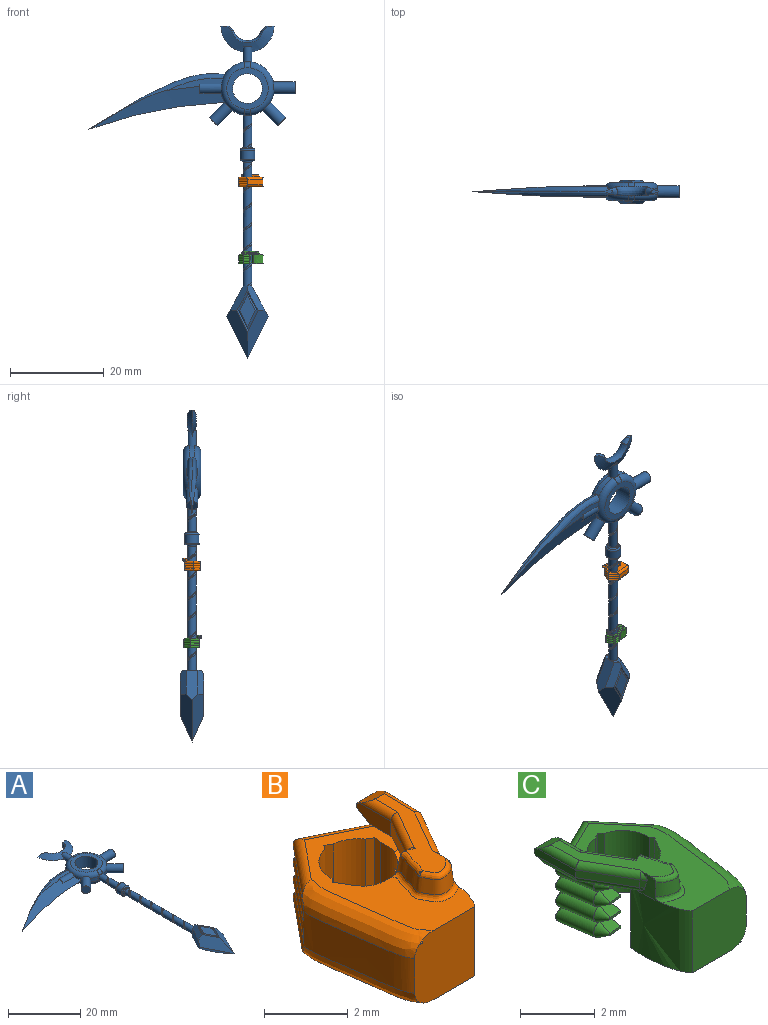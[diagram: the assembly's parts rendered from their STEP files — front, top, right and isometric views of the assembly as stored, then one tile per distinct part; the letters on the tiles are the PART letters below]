
ASSEMBLY  parts=3 mates=2
PART A: 95 faces, bbox 47.1x71.3x5.4 mm
  f0: cylinder r=0.95mm len=6.92mm, axis (0,1,0), area 36.3mm2, adj f1,f2,f3,f6,f20,f23,f67,f69
  f1: bspline ~8.16x2.41mm, area 3.9mm2, adj f0,f2,f3,f37,f38,f67,f68,f69
  f2: bspline ~8.15x2.45mm, area 3.9mm2, adj f0,f1,f20,f37,f38,f67
  f3: cylinder r=5.71mm len=2.59mm, axis (0,0,-1), area 3.2mm2, adj f0,f1,f12,f13,f35,f37
  f4: cylinder r=5.71mm len=2.11mm, axis (0,0,-1), area 0.8mm2, adj f13,f35,f40,f44
  f5: cylinder r=3.17mm len=6.35mm, axis (0,0,-1), area 76mm2, adj f16,f17
  f6: cylinder r=5.71mm len=2.59mm, axis (0,0,-1), area 3.2mm2, adj f0,f8,f9,f33
  f7: cylinder r=5.71mm len=2.11mm, axis (0,0,-1), area 2.6mm2, adj f8,f9,f25,f33
  f8: torus R=4.45mm, axis (0,0,1), area 28.3mm2, adj f6,f7,f15,f17,f20,f21,f25,f33
  f9: torus R=4.45mm, axis (0,0,1), area 28.3mm2, adj f6,f7,f15,f16,f22,f23,f25,f33
  f10: cylinder r=5.71mm len=4.27mm, axis (0,0,-1), area 6.4mm2, adj f12,f13,f19,f41,f42
  f11: cylinder r=5.71mm len=2.11mm, axis (0,0,-1), area 0.8mm2, adj f12,f35,f39,f45
  f12: torus R=4.45mm, axis (0,0,1), area 27.6mm2, adj f3,f10,f11,f17,f20,f21,f32,f35
  f13: torus R=4.45mm, axis (0,0,1), area 27.7mm2, adj f3,f4,f10,f16,f22,f23,f31,f35
  f14: plane 1.74x0.58mm, normal (0,1,0), area 0.4mm2, adj f19,f26
  f15: cylinder r=5.71mm len=4.87mm, axis (0,0,-1), area 8.6mm2, adj f8,f9,f19,f25
  f16: plane 8.97x8.89mm, normal (0,0,1), area 30.4mm2, adj f5,f9,f13,f22,f23
  f17: plane 8.97x8.89mm, normal (0,0,-1), area 30.4mm2, adj f5,f8,f12,f20,f21
  f18: plane 1.66x0.52mm, normal (0,1,0), area 0.4mm2, adj f19,f27
  f19: cylinder r=0.95mm len=3.3mm, axis (0,1,0), area 18.3mm2, adj f10,f14,f15,f18,f21,f22,f26,f27
  f20: bspline ~1.53x1.35mm, area 2.3mm2, adj f0,f2,f8,f12,f17,f37
  f21: bspline ~1.42x1.3mm, area 2.3mm2, adj f8,f12,f17,f19
  f22: bspline ~1.42x1.3mm, area 2.3mm2, adj f9,f13,f16,f19
  f23: bspline ~1.42x1.3mm, area 2.3mm2, adj f0,f9,f13,f16
  f24: plane 2.54x2.54mm, normal (1,0,0), area 5.1mm2, adj f25
  f25: cylinder r=1.27mm len=4.58mm, axis (-1,0,0), area 36.3mm2, adj f7,f8,f9,f15,f24
  f26: bspline ~11.33x5.46mm, area 29.7mm2, adj f14,f19,f27,f28,f29,f30,f93,f94
  f27: bspline ~11.33x5.46mm, area 30.2mm2, adj f18,f19,f26,f28,f29,f30,f93,f94
  f28: plane 1.88x1.27mm, normal (0.01,1,0), area 0.8mm2, adj f26,f27,f94
  f29: plane 1.84x1.25mm, normal (0.01,1,0), area 0.7mm2, adj f26,f27,f93
  f30: bspline ~7.14x7.14mm, area 18.5mm2, adj f26,f27,f93,f94
  f31: plane 12.18x2.8mm, normal (0,0,1), area 11.7mm2, adj f13,f40,f41,f43,f44
  f32: plane 12.19x2.81mm, normal (0,0,-1), area 11.7mm2, adj f12,f39,f42,f45,f46
  f33: cylinder r=1.27mm len=5.04mm, axis (-0.71,0.71,0), area 36.3mm2, adj f6,f7,f8,f9,f34
  f34: plane 2.54x1.8mm, normal (0.71,-0.71,0), area 5.1mm2, adj f33
  f35: cylinder r=1.27mm len=5.06mm, axis (0.71,0.71,0), area 36.2mm2, adj f3,f4,f11,f12,f13,f36
  f36: plane 2.54x1.8mm, normal (-0.71,-0.71,0), area 5.1mm2, adj f35
  f37: bspline ~2.13x1.59mm, area 0.5mm2, adj f1,f2,f3,f12,f20,f38
  f38: plane 0.71x0.37mm, normal (0,0,-1), area 0.1mm2, adj f1,f2,f37
  f39: bspline ~33.29x10.15mm, area 73.1mm2, adj f11,f32,f40,f42,f45,f46
  f40: bspline ~33.29x10.15mm, area 73mm2, adj f4,f31,f39,f41,f43,f44
  f41: bspline ~30.28x13.43mm, area 35.4mm2, adj f10,f13,f31,f40,f42
  f42: bspline ~30.28x13.43mm, area 35.4mm2, adj f10,f12,f32,f39,f41
  f43: plane 1.87x0.64mm, normal (-1,0,0), area 0.5mm2, adj f31,f40,f44
  f44: cylinder r=1.27mm len=4.58mm, axis (1,0,0), area 10.1mm2, adj f4,f13,f31,f40,f43
  f45: cylinder r=1.27mm len=4.58mm, axis (1,0,0), area 10.1mm2, adj f11,f12,f32,f39,f46
  f46: plane 1.87x0.64mm, normal (-1,0,0), area 0.5mm2, adj f32,f39,f45
  f47: plane 2.57x2.57mm, normal (0,1,0), area 0.2mm2, adj f67,f68,f69,f74
  f48: plane 2.57x2.57mm, normal (0,-1,0), area 0.2mm2, adj f70,f71,f72,f73
  f49: cylinder r=1.59mm len=3.18mm, axis (0,-1,0), area 19.3mm2, adj f73,f74
  f50: plane 10.2x4.46mm, normal (-0.63,-0.32,0.71), area 28.3mm2, adj f51,f53,f57,f58,f78
  f51: plane 10.2x4.46mm, normal (-0.63,-0.32,-0.71), area 28.3mm2, adj f50,f52,f55,f58,f84
  f52: plane 5.16x3.72mm, normal (-0.62,0.34,-0.71), area 10.1mm2, adj f51,f54,f58,f59,f85
  f53: plane 10.2x4.46mm, normal (0.63,-0.32,0.71), area 28.3mm2, adj f50,f55,f56,f61,f79
  f54: plane 5.16x3.72mm, normal (0.62,0.34,-0.71), area 10.1mm2, adj f52,f55,f60,f61,f86
  f55: plane 10.2x4.46mm, normal (0.63,-0.32,-0.71), area 28.3mm2, adj f51,f53,f54,f61,f91
  f56: plane 5.16x3.72mm, normal (0.62,0.34,0.71), area 10.1mm2, adj f53,f57,f61,f62,f80
  f57: plane 5.16x3.72mm, normal (-0.62,0.34,0.71), area 10.1mm2, adj f50,f56,f58,f63,f81
  f58: plane 6.48x3.56mm, normal (-0.88,0.48,0), area 16.7mm2, adj f50,f51,f52,f57,f59,f63,f66
  f59: plane 1.93x0.96mm, normal (-0.06,1,0), area 0.9mm2, adj f52,f58,f60,f66
  f60: plane 1.93x0.96mm, normal (0.06,1,0), area 0.9mm2, adj f54,f59,f61,f66
  f61: plane 6.48x3.56mm, normal (0.88,0.48,0), area 16.7mm2, adj f53,f54,f55,f56,f60,f62,f66
  f62: plane 1.94x0.96mm, normal (0.06,1,0), area 0.9mm2, adj f56,f61,f63,f64,f65,f66
  f63: plane 1.93x0.95mm, normal (-0.06,1,0), area 0.9mm2, adj f57,f58,f62,f64,f66
  f64: bspline ~28x2.45mm, area 13.4mm2, adj f62,f63,f65,f66,f70,f71,f72
  f65: bspline ~28.02x2.41mm, area 13.8mm2, adj f62,f64,f66,f71
  f66: cylinder r=0.95mm len=26.59mm, axis (0,1,0), area 134.4mm2, adj f58,f59,f60,f61,f62,f63,f64,f65
  f67: bspline ~0.85x0.81mm, area 0.2mm2, adj f0,f1,f2,f47,f68,f69
  f68: bspline ~0.61x0.46mm, area 0.1mm2, adj f1,f47,f67,f69
  f69: torus R=1.26mm, axis (0,-1,0), area 3mm2, adj f0,f1,f47,f67,f68
  f70: bspline ~0.57x0.49mm, area 0.1mm2, adj f48,f64,f71,f72
  f71: bspline ~0.85x0.75mm, area 0.2mm2, adj f48,f64,f65,f66,f70,f72
  f72: torus R=1.26mm, axis (0,-1,0), area 3mm2, adj f48,f64,f66,f70,f71
  f73: torus R=1.28mm, axis (0,-1,0), area 4.4mm2, adj f48,f49
  f74: torus R=1.28mm, axis (0,-1,0), area 4.4mm2, adj f47,f49
  f75: plane 3.66x2mm, normal (-0.62,0.34,0.71), area 1.4mm2, adj f76,f81,f82,f83
  f76: plane 3.66x2mm, normal (0.62,0.34,0.71), area 1.4mm2, adj f75,f77,f80,f83
  f77: plane 3.96x2mm, normal (0.63,-0.32,0.71), area 1.5mm2, adj f76,f79,f82,f83
  f78: plane 4.53x2.28mm, normal (0.63,0.32,0.71), area 1.7mm2, adj f50,f79,f81,f82
  f79: plane 4.53x2.28mm, normal (-0.63,0.32,0.71), area 1.7mm2, adj f53,f77,f78,f80
  f80: plane 4.18x2.28mm, normal (-0.62,-0.34,0.71), area 1.6mm2, adj f56,f76,f79,f81
  f81: plane 4.18x2.28mm, normal (0.62,-0.34,0.71), area 1.6mm2, adj f57,f75,f78,f80
  f82: plane 3.96x2mm, normal (-0.63,-0.32,0.71), area 1.5mm2, adj f75,f77,f78,f83
  f83: plane 6.52x3.42mm, normal (0,0,1), area 11.1mm2, adj f75,f76,f77,f82
  f84: plane 4.53x2.28mm, normal (0.63,0.32,-0.71), area 1.7mm2, adj f51,f85,f90,f91
  f85: plane 4.18x2.28mm, normal (0.62,-0.34,-0.71), area 1.6mm2, adj f52,f84,f86,f89
  f86: plane 4.18x2.28mm, normal (-0.62,-0.34,-0.71), area 1.6mm2, adj f54,f85,f88,f91
  f87: plane 3.96x2mm, normal (0.63,-0.32,-0.71), area 1.5mm2, adj f88,f90,f91,f92
  f88: plane 3.66x2mm, normal (0.62,0.34,-0.71), area 1.4mm2, adj f86,f87,f89,f92
  f89: plane 3.66x2mm, normal (-0.62,0.34,-0.71), area 1.4mm2, adj f85,f88,f90,f92
  f90: plane 3.96x2mm, normal (-0.63,-0.32,-0.71), area 1.5mm2, adj f84,f87,f89,f92
  f91: plane 4.53x2.28mm, normal (-0.63,0.32,-0.71), area 1.7mm2, adj f55,f84,f86,f87
  f92: plane 6.52x3.42mm, normal (0,0,-1), area 11.1mm2, adj f87,f88,f89,f90
  f93: bspline ~2.68x1.63mm, area 2.6mm2, adj f26,f27,f29,f30
  f94: bspline ~2.79x1.69mm, area 2.8mm2, adj f26,f27,f28,f30
PART B: 79 faces, bbox 4.3x5.7x2.9 mm
  f0: plane 4.84x2.76mm, normal (0,0,-1), area 6.7mm2, adj f5,f6,f7,f8,f9,f10,f12,f16
  f1: plane 0.22x0.13mm, normal (-0.98,0.2,0), area 0mm2, adj f10,f19,f23,f76
  f2: plane 0.22x0.13mm, normal (-0.98,0.2,0), area 0mm2, adj f25,f29,f30,f76
  f3: plane 0.22x0.13mm, normal (-0.98,0.2,0), area 0mm2, adj f32,f36,f37,f76
  f4: plane 0.22x0.13mm, normal (-0.98,0.2,0), area 0mm2, adj f39,f43,f44,f76
  f5: plane 2.03x0.23mm, normal (-0.98,0.2,0), area 0.5mm2, adj f0,f7,f11,f76
  f6: plane 2.03x0.21mm, normal (-0.51,-0.86,0), area 0.5mm2, adj f0,f9,f11,f78
  f7: plane 2.03x0.2mm, normal (-0.51,-0.86,0), area 0.5mm2, adj f0,f5,f11,f78
  f8: plane 2.03x0.12mm, normal (0.8,-0.6,0), area 0.3mm2, adj f0,f11,f12,f77
  f9: plane 2.03x0.14mm, normal (0.8,-0.6,0), area 0.4mm2, adj f0,f6,f11,f77
  f10: plane 0.47x0.41mm, normal (-0.04,-0.5,-0.87), area 0.2mm2, adj f0,f1,f19,f24,f76
  f11: plane 4.94x2.78mm, normal (0,0,1), area 5.2mm2, adj f5,f6,f7,f8,f9,f12,f16,f17
  f12: extruded ~2.03x2.02mm, area 5mm2, adj f0,f8,f11,f17,f48,f69
  f13: extruded ~0.41x0.37mm, area 0.1mm2, adj f18,f35,f42,f46
  f14: extruded ~0.51x0.37mm, area 0.1mm2, adj f18,f28,f35
  f15: extruded ~0.41x0.37mm, area 0.1mm2, adj f18,f22,f28,f47
  f16: plane 2.18x2.18mm, normal (0,-1,0), area 4mm2, adj f0,f11,f17,f18,f46,f47
  f17: extruded ~2.05x2.01mm, area 4.2mm2, adj f0,f11,f12,f16,f48,f70,f72
  f18: extruded ~3.28x1.02mm, area 3.4mm2, adj f13,f14,f15,f16,f46,f47
  f19: plane 0.48x0.07mm, normal (-0.07,-1,0), area 0mm2, adj f1,f10,f23,f24
  f20: cylinder r=0.25mm len=1.12mm, axis (0.14,0.99,0), area 0.9mm2, adj f0,f21,f24,f26
  f21: cylinder r=0.25mm len=1.76mm, axis (-0.9,0.44,0), area 1.5mm2, adj f0,f20,f22,f27
  f22: cylinder r=0.25mm len=2.02mm, axis (-0.64,-0.77,0), area 1.7mm2, adj f0,f15,f21,f28,f47
  f23: plane 0.47x0.41mm, normal (-0.04,-0.5,0.87), area 0.2mm2, adj f1,f19,f24,f29,f76
  f24: bspline ~0.52x0.38mm, area 0.2mm2, adj f10,f19,f20,f23
  f25: plane 0.48x0.07mm, normal (-0.07,-1,0), area 0mm2, adj f2,f29,f30,f31
  f26: cylinder r=0.25mm len=1.12mm, axis (0.14,0.99,0), area 0.9mm2, adj f20,f27,f31,f33
  f27: cylinder r=0.25mm len=1.76mm, axis (-0.9,0.44,0), area 1.5mm2, adj f21,f26,f28,f34
  f28: cylinder r=0.25mm len=1.88mm, axis (-0.64,-0.77,0), area 1.7mm2, adj f14,f15,f22,f27,f35
  f29: plane 0.47x0.41mm, normal (-0.04,-0.5,-0.87), area 0.2mm2, adj f2,f23,f25,f31,f76
  f30: plane 0.47x0.41mm, normal (-0.04,-0.5,0.87), area 0.2mm2, adj f2,f25,f31,f36,f76
  f31: bspline ~0.52x0.38mm, area 0.2mm2, adj f25,f26,f29,f30
  f32: plane 0.48x0.07mm, normal (-0.07,-1,0), area 0mm2, adj f3,f36,f37,f38
  f33: cylinder r=0.25mm len=1.12mm, axis (0.14,0.99,0), area 0.9mm2, adj f26,f34,f38,f40
  f34: cylinder r=0.25mm len=1.76mm, axis (-0.9,0.44,0), area 1.5mm2, adj f27,f33,f35,f41
  f35: cylinder r=0.25mm len=1.88mm, axis (-0.64,-0.77,0), area 1.7mm2, adj f13,f14,f28,f34,f42
  f36: plane 0.47x0.41mm, normal (-0.04,-0.5,-0.87), area 0.2mm2, adj f3,f30,f32,f38,f76
  f37: plane 0.47x0.41mm, normal (-0.04,-0.5,0.87), area 0.2mm2, adj f3,f32,f38,f43,f76
  f38: bspline ~0.52x0.38mm, area 0.2mm2, adj f32,f33,f36,f37
  f39: plane 0.48x0.07mm, normal (-0.07,-1,0), area 0mm2, adj f4,f43,f44,f45
  f40: cylinder r=0.25mm len=1.3mm, axis (-0.14,-0.99,0), area 1mm2, adj f11,f33,f41,f45,f48
  f41: cylinder r=0.25mm len=2.11mm, axis (0.9,-0.44,0), area 1.7mm2, adj f11,f34,f40,f42,f48
  f42: cylinder r=0.25mm len=2.02mm, axis (0.64,0.77,0), area 1.7mm2, adj f11,f13,f35,f41,f46
  f43: plane 0.47x0.41mm, normal (-0.04,-0.5,-0.87), area 0.2mm2, adj f4,f37,f39,f45,f76
  f44: plane 0.48x0.41mm, normal (-0.04,-0.5,0.87), area 0.2mm2, adj f4,f11,f39,f45,f48,f76
  f45: bspline ~0.52x0.38mm, area 0.2mm2, adj f39,f40,f43,f44
  f46: bspline ~4.29x1.18mm, area 2.8mm2, adj f11,f13,f16,f18,f42
  f47: bspline ~4.29x1.18mm, area 2.8mm2, adj f0,f15,f16,f18,f22
  f48: plane 2.43x1.13mm, normal (0,0,-1), area 1mm2, adj f12,f17,f40,f41,f44,f54,f56,f61
  f49: extruded ~0.25x0.05mm, area 0mm2, adj f51,f54,f57,f69
  f50: plane 0.25x0.17mm, normal (0.87,-0.5,0), area 0mm2, adj f52,f55,f58,f70
  f51: bspline ~1.04x0.65mm, area 0mm2, adj f49,f62,f66,f69
  f52: cylinder r=0.19mm len=0.24mm, axis (-0.5,-0.87,0), area 0mm2, adj f50,f53,f70
  f53: cylinder r=0.19mm len=1.64mm, axis (-0.5,-0.87,0), area 0.5mm2, adj f52,f58,f62,f67,f70
  f54: bspline ~3.19x1.76mm, area 0.3mm2, adj f11,f48,f49,f57,f61,f69
  f55: cylinder r=0.19mm len=0.14mm, axis (0.5,0.87,0), area 0mm2, adj f50,f56,f70
  f56: cylinder r=0.19mm len=1.64mm, axis (0.5,0.87,0), area 0.5mm2, adj f48,f55,f58,f68,f70
  f57: plane 1.26x0.73mm, normal (-0.87,0.5,0), area 0.5mm2, adj f49,f54,f61,f66
  f58: plane 1.54x0.89mm, normal (0.87,-0.5,0), area 0.5mm2, adj f50,f53,f56,f59
  f59: plane 1.54x0.25mm, normal (1,-0.03,0), area 0.4mm2, adj f58,f60,f63,f64,f67,f68
  f60: plane 0.7x0.13mm, normal (0,1,0), area 0.1mm2, adj f59,f61,f63,f64
  f61: plane 1.42x0.45mm, normal (-1,0,0), area 0.5mm2, adj f11,f48,f54,f57,f60,f63,f64,f65
  f62: plane 3.34x1.7mm, normal (0,0,1), area 1.5mm2, adj f51,f53,f64,f65,f66,f67,f69,f70
  f63: plane 0.84x0.58mm, normal (0,0.5,-0.87), area 0.3mm2, adj f48,f59,f60,f61,f68
  f64: plane 0.84x0.58mm, normal (0,0.5,0.87), area 0.3mm2, adj f59,f60,f61,f62,f65,f67
  f65: cylinder r=0.19mm len=1.1mm, axis (0,1,0), area 0.3mm2, adj f61,f62,f64,f66
  f66: cylinder r=0.19mm len=1.4mm, axis (0.5,0.87,0), area 0.4mm2, adj f51,f57,f62,f65
  f67: cylinder r=0.19mm len=1.44mm, axis (-0.03,-1,0), area 0.4mm2, adj f53,f59,f62,f64
  f68: cylinder r=0.19mm len=1.44mm, axis (0.03,1,0), area 0.4mm2, adj f48,f56,f59,f63
  f69: bspline ~0.7x0.69mm, area 0.2mm2, adj f12,f49,f51,f54,f62,f71,f72,f75
  f70: bspline ~0.95x0.69mm, area 0.3mm2, adj f17,f50,f52,f53,f55,f56,f62,f71
  f71: bspline ~1.52x1.01mm, area 0.9mm2, adj f69,f70,f72,f73,f74,f75
  f72: bspline ~1.93x1.43mm, area 0.4mm2, adj f11,f17,f69,f70,f71
  f73: bspline ~1.05x0.52mm, area 0.2mm2, adj f62,f70,f71,f74
  f74: bspline ~0.13x0.11mm, area 0mm2, adj f71,f73,f75
  f75: bspline ~1.01x0.41mm, area 0.2mm2, adj f62,f69,f71,f74
  f76: cylinder r=0.95mm len=2.03mm, axis (0,0,-1), area 1.4mm2, adj f0,f1,f2,f3,f4,f5,f10,f11
  f77: cylinder r=0.95mm len=2.03mm, axis (0,0,-1), area 2.7mm2, adj f0,f8,f9,f11
  f78: cylinder r=0.95mm len=2.03mm, axis (0,0,-1), area 1.7mm2, adj f0,f6,f7,f11
PART C: 79 faces, bbox 4.3x5.7x2.9 mm
  f0: plane 4.84x2.76mm, normal (0,0,-1), area 6.7mm2, adj f5,f6,f7,f8,f9,f10,f12,f16
  f1: plane 0.22x0.13mm, normal (0.98,0.2,0), area 0mm2, adj f10,f19,f23,f76
  f2: plane 0.22x0.13mm, normal (0.98,0.2,0), area 0mm2, adj f25,f29,f30,f76
  f3: plane 0.22x0.13mm, normal (0.98,0.2,0), area 0mm2, adj f32,f36,f37,f76
  f4: plane 0.22x0.13mm, normal (0.98,0.2,0), area 0mm2, adj f39,f43,f44,f76
  f5: plane 2.03x0.23mm, normal (0.98,0.2,0), area 0.5mm2, adj f0,f7,f11,f76
  f6: plane 2.03x0.21mm, normal (0.51,-0.86,0), area 0.5mm2, adj f0,f9,f11,f78
  f7: plane 2.03x0.2mm, normal (0.51,-0.86,0), area 0.5mm2, adj f0,f5,f11,f78
  f8: plane 2.03x0.12mm, normal (-0.8,-0.6,0), area 0.3mm2, adj f0,f11,f12,f77
  f9: plane 2.03x0.14mm, normal (-0.8,-0.6,0), area 0.4mm2, adj f0,f6,f11,f77
  f10: plane 0.47x0.41mm, normal (0.04,-0.5,-0.87), area 0.2mm2, adj f0,f1,f19,f24,f76
  f11: plane 4.94x2.78mm, normal (0,0,1), area 5.2mm2, adj f5,f6,f7,f8,f9,f12,f16,f17
  f12: extruded ~2.03x2.02mm, area 5mm2, adj f0,f8,f11,f17,f48,f69
  f13: extruded ~0.41x0.37mm, area 0.1mm2, adj f18,f35,f42,f46
  f14: extruded ~0.51x0.37mm, area 0.1mm2, adj f18,f28,f35
  f15: extruded ~0.41x0.37mm, area 0.1mm2, adj f18,f22,f28,f47
  f16: plane 2.18x2.18mm, normal (0,-1,0), area 4mm2, adj f0,f11,f17,f18,f46,f47
  f17: extruded ~2.05x2.01mm, area 4.2mm2, adj f0,f11,f12,f16,f48,f70,f72
  f18: extruded ~3.28x1.02mm, area 3.4mm2, adj f13,f14,f15,f16,f46,f47
  f19: plane 0.48x0.07mm, normal (0.07,-1,0), area 0mm2, adj f1,f10,f23,f24
  f20: cylinder r=0.25mm len=1.12mm, axis (-0.14,0.99,0), area 0.9mm2, adj f0,f21,f24,f26
  f21: cylinder r=0.25mm len=1.76mm, axis (0.9,0.44,0), area 1.5mm2, adj f0,f20,f22,f27
  f22: cylinder r=0.25mm len=2.02mm, axis (0.64,-0.77,0), area 1.7mm2, adj f0,f15,f21,f28,f47
  f23: plane 0.47x0.41mm, normal (0.04,-0.5,0.87), area 0.2mm2, adj f1,f19,f24,f29,f76
  f24: bspline ~0.52x0.38mm, area 0.2mm2, adj f10,f19,f20,f23
  f25: plane 0.48x0.07mm, normal (0.07,-1,0), area 0mm2, adj f2,f29,f30,f31
  f26: cylinder r=0.25mm len=1.12mm, axis (-0.14,0.99,0), area 0.9mm2, adj f20,f27,f31,f33
  f27: cylinder r=0.25mm len=1.76mm, axis (0.9,0.44,0), area 1.5mm2, adj f21,f26,f28,f34
  f28: cylinder r=0.25mm len=1.88mm, axis (0.64,-0.77,0), area 1.7mm2, adj f14,f15,f22,f27,f35
  f29: plane 0.47x0.41mm, normal (0.04,-0.5,-0.87), area 0.2mm2, adj f2,f23,f25,f31,f76
  f30: plane 0.47x0.41mm, normal (0.04,-0.5,0.87), area 0.2mm2, adj f2,f25,f31,f36,f76
  f31: bspline ~0.52x0.38mm, area 0.2mm2, adj f25,f26,f29,f30
  f32: plane 0.48x0.07mm, normal (0.07,-1,0), area 0mm2, adj f3,f36,f37,f38
  f33: cylinder r=0.25mm len=1.12mm, axis (-0.14,0.99,0), area 0.9mm2, adj f26,f34,f38,f40
  f34: cylinder r=0.25mm len=1.76mm, axis (0.9,0.44,0), area 1.5mm2, adj f27,f33,f35,f41
  f35: cylinder r=0.25mm len=1.88mm, axis (0.64,-0.77,0), area 1.7mm2, adj f13,f14,f28,f34,f42
  f36: plane 0.47x0.41mm, normal (0.04,-0.5,-0.87), area 0.2mm2, adj f3,f30,f32,f38,f76
  f37: plane 0.47x0.41mm, normal (0.04,-0.5,0.87), area 0.2mm2, adj f3,f32,f38,f43,f76
  f38: bspline ~0.52x0.38mm, area 0.2mm2, adj f32,f33,f36,f37
  f39: plane 0.48x0.07mm, normal (0.07,-1,0), area 0mm2, adj f4,f43,f44,f45
  f40: cylinder r=0.25mm len=1.3mm, axis (0.14,-0.99,0), area 1mm2, adj f11,f33,f41,f45,f48
  f41: cylinder r=0.25mm len=2.11mm, axis (-0.9,-0.44,0), area 1.7mm2, adj f11,f34,f40,f42,f48
  f42: cylinder r=0.25mm len=2.02mm, axis (-0.64,0.77,0), area 1.7mm2, adj f11,f13,f35,f41,f46
  f43: plane 0.47x0.41mm, normal (0.04,-0.5,-0.87), area 0.2mm2, adj f4,f37,f39,f45,f76
  f44: plane 0.48x0.41mm, normal (0.04,-0.5,0.87), area 0.2mm2, adj f4,f11,f39,f45,f48,f76
  f45: bspline ~0.52x0.38mm, area 0.2mm2, adj f39,f40,f43,f44
  f46: bspline ~4.29x1.18mm, area 2.8mm2, adj f11,f13,f16,f18,f42
  f47: bspline ~4.29x1.18mm, area 2.8mm2, adj f0,f15,f16,f18,f22
  f48: plane 2.43x1.13mm, normal (0,0,-1), area 1mm2, adj f12,f17,f40,f41,f44,f54,f56,f61
  f49: extruded ~0.25x0.05mm, area 0mm2, adj f51,f54,f57,f69
  f50: plane 0.25x0.17mm, normal (-0.87,-0.5,0), area 0mm2, adj f52,f55,f58,f70
  f51: bspline ~1.06x0.66mm, area 0mm2, adj f49,f62,f66,f69
  f52: cylinder r=0.19mm len=0.24mm, axis (0.5,-0.87,0), area 0mm2, adj f50,f53,f70
  f53: cylinder r=0.19mm len=1.64mm, axis (0.5,-0.87,0), area 0.5mm2, adj f52,f58,f62,f67,f70
  f54: bspline ~3.19x1.76mm, area 0.3mm2, adj f11,f48,f49,f57,f61,f69
  f55: cylinder r=0.19mm len=0.14mm, axis (-0.5,0.87,0), area 0mm2, adj f50,f56,f70
  f56: cylinder r=0.19mm len=1.64mm, axis (-0.5,0.87,0), area 0.5mm2, adj f48,f55,f58,f68,f70
  f57: plane 1.26x0.73mm, normal (0.87,0.5,0), area 0.5mm2, adj f49,f54,f61,f66
  f58: plane 1.54x0.89mm, normal (-0.87,-0.5,0), area 0.5mm2, adj f50,f53,f56,f59
  f59: plane 1.54x0.25mm, normal (-1,-0.03,0), area 0.4mm2, adj f58,f60,f63,f64,f67,f68
  f60: plane 0.7x0.13mm, normal (0,1,0), area 0.1mm2, adj f59,f61,f63,f64
  f61: plane 1.42x0.45mm, normal (1,0,0), area 0.5mm2, adj f11,f48,f54,f57,f60,f63,f64,f65
  f62: plane 3.34x1.7mm, normal (0,0,1), area 1.5mm2, adj f51,f53,f64,f65,f66,f67,f69,f70
  f63: plane 0.84x0.58mm, normal (0,0.5,-0.87), area 0.3mm2, adj f48,f59,f60,f61,f68
  f64: plane 0.84x0.58mm, normal (0,0.5,0.87), area 0.3mm2, adj f59,f60,f61,f62,f65,f67
  f65: cylinder r=0.19mm len=1.1mm, axis (0,1,0), area 0.3mm2, adj f61,f62,f64,f66
  f66: cylinder r=0.19mm len=1.4mm, axis (-0.5,0.87,0), area 0.4mm2, adj f51,f57,f62,f65
  f67: cylinder r=0.19mm len=1.44mm, axis (0.03,-1,0), area 0.4mm2, adj f53,f59,f62,f64
  f68: cylinder r=0.19mm len=1.44mm, axis (-0.03,1,0), area 0.4mm2, adj f48,f56,f59,f63
  f69: bspline ~0.7x0.69mm, area 0.2mm2, adj f12,f49,f51,f54,f62,f71,f72,f75
  f70: bspline ~0.95x0.69mm, area 0.3mm2, adj f17,f50,f52,f53,f55,f56,f62,f71
  f71: bspline ~1.52x1.01mm, area 0.9mm2, adj f69,f70,f72,f73,f74,f75
  f72: bspline ~1.93x1.43mm, area 0.4mm2, adj f11,f17,f69,f70,f71
  f73: bspline ~1.05x0.52mm, area 0.2mm2, adj f62,f70,f71,f74
  f74: bspline ~0.13x0.11mm, area 0mm2, adj f71,f73,f75
  f75: bspline ~1.01x0.41mm, area 0.2mm2, adj f62,f69,f71,f74
  f76: cylinder r=0.95mm len=2.03mm, axis (0,0,-1), area 1.4mm2, adj f0,f1,f2,f3,f4,f5,f10,f11
  f77: cylinder r=0.95mm len=2.03mm, axis (0,0,-1), area 2.7mm2, adj f0,f8,f9,f11
  f78: cylinder r=0.95mm len=2.03mm, axis (0,0,-1), area 1.7mm2, adj f0,f6,f7,f11
PLACE A rot(axis=(1,0,0),90deg) t=(-9.89,-21.28,26.33)mm fixed
PLACE B rot(axis=(0,0,1),90deg) t=(-9.89,-21.28,-3.63)mm
PLACE C rot(axis=(0,0,1),90deg) t=(-9.89,-21.28,-20.13)mm
MATE slider B.f76 <-> A.f0  axis (0,0,-1) through (-9.89,-21.28,-1.6)mm
MATE slider C.f76 <-> A.f0  axis (0,0,-1) through (-9.89,-21.28,-18.1)mm
